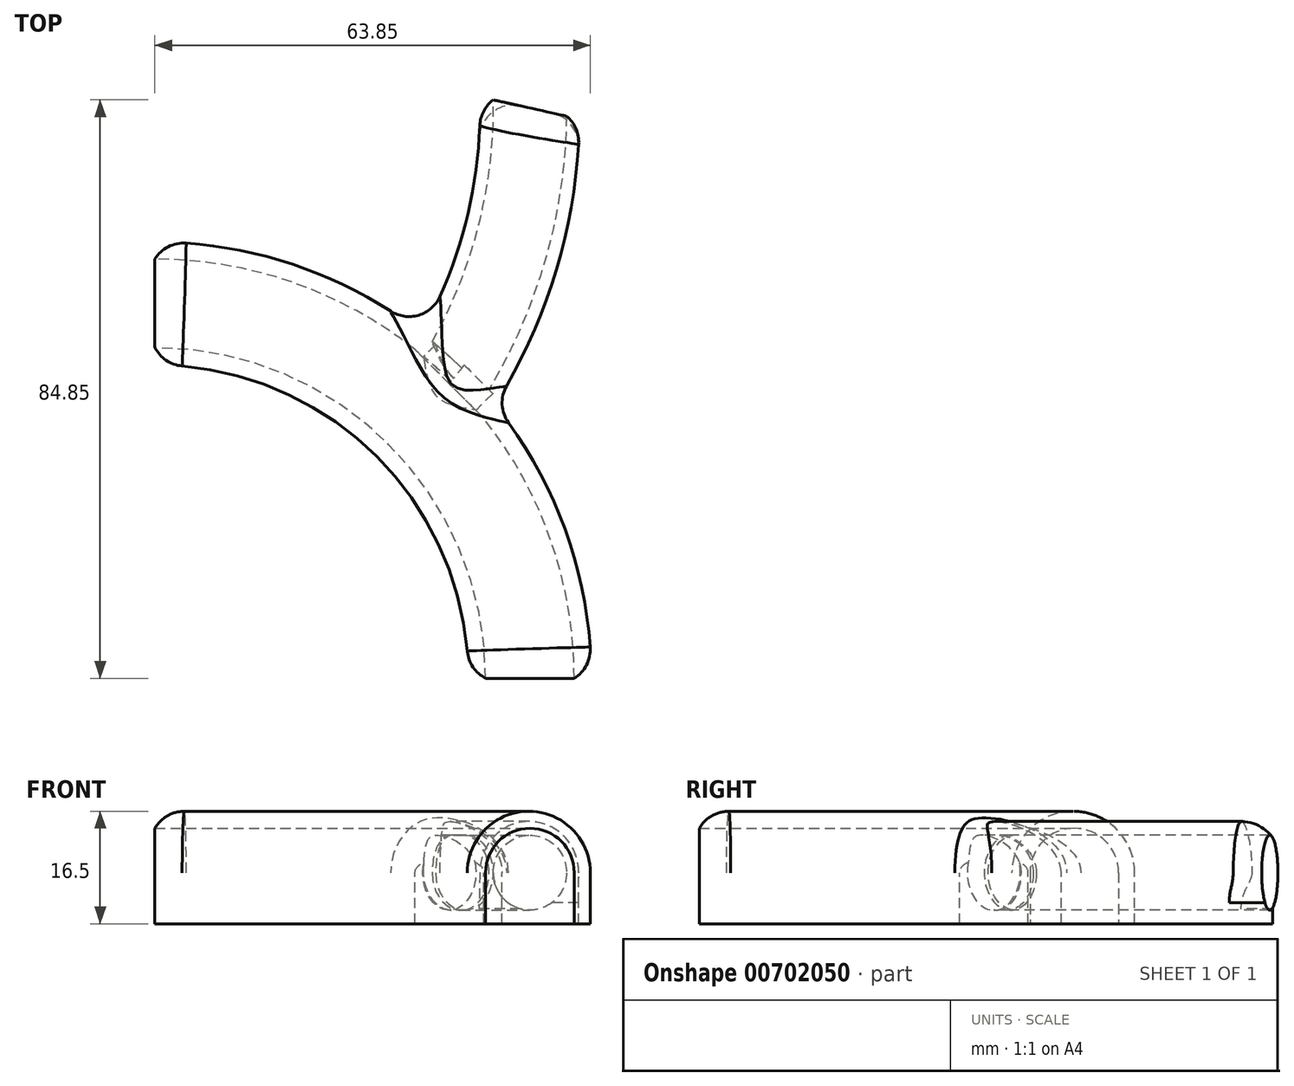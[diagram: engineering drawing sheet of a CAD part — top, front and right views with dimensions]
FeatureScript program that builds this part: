
annotation { "Feature Type Name" : "Feature", "Feature Type Description" : "" }
export const myFeature = defineFeature(function(context is Context, id is Id, definition is map)
    precondition{}
    {
        {
            var Q0;
            Q0=qCreatedBy(makeId("Top.planeOp"),FACE);
            var sketch = newSketch(context, id + "F0", { "sketchPlane" : qUnion([Q0])});
            skArc(sketch, "E0", {"start": v(55, 0) * mm, "mid": v(38.9, 38.9) * mm, "end": v(0, 55) * mm});
            skLineSegment(sketch, "E1", {"start": v(0, 0) * mm, "end": v(43.2, 43.2) * mm, "construction": true});
            skLineSegment(sketch, "E2", {"start": v(55, 0) * mm, "end": v(55, 83.67) * mm, "construction": true});
            skArc(sketch, "E3", {"start": v(43.2, 43.2) * mm, "mid": v(51.99, 62.59) * mm, "end": v(55, 83.67) * mm});
            skSolve(sketch);
        }
        {
            var Q0;
            Q0=qCreatedBy(makeId("Front.planeOp"),FACE);
            var sketch = newSketch(context, id + "F1", { "sketchPlane" : qUnion([Q0])});
            skArc(sketch, "E4", {"start": v(64, 0) * mm, "mid": v(55, 9) * mm, "end": v(46, 0) * mm});
            skLineSegment(sketch, "E5", {"start": v(55, 0) * mm, "end": v(64, 0) * mm, "construction": true});
            skLineSegment(sketch, "E6", {"start": v(55, 0) * mm, "end": v(46, 0) * mm, "construction": true});
            skLineSegment(sketch, "E7", {"start": v(55, 0) * mm, "end": v(55, -9) * mm, "construction": true});
            skLineSegment(sketch, "E8.bottom", {"start": v(46, 0) * mm, "end": v(48.5, 0) * mm});
            skLineSegment(sketch, "E8.left", {"start": v(46, 0) * mm, "end": v(46, -7.5) * mm});
            skArc(sketch, "E9", {"start": v(61.5, 0) * mm, "mid": v(55, 6.5) * mm, "end": v(48.5, 0) * mm});
            skLineSegment(sketch, "E10", {"start": v(55, -7.5) * mm, "end": v(46, -7.5) * mm, "construction": true});
            skLineSegment(sketch, "E11", {"start": v(48.5, 0) * mm, "end": v(48.5, -7.5) * mm});
            skLineSegment(sketch, "E12", {"start": v(48.5, -7.5) * mm, "end": v(46, -7.5) * mm});
            skLineSegment(sketch, "E13.MirrorCS", {"start": v(61.5, 0) * mm, "end": v(61.5, -7.5) * mm});
            skLineSegment(sketch, "E14.MirrorCS", {"start": v(61.5, -7.5) * mm, "end": v(64, -7.5) * mm});
            skLineSegment(sketch, "E15.MirrorCS", {"start": v(64, 0) * mm, "end": v(64, -7.5) * mm});
            skLineSegment(sketch, "E16.trimOffspring", {"start": v(61.5, 0) * mm, "end": v(64, 0) * mm});
            skSolve(sketch);
        }
        {
            var Q0;
            Q0=makeQuery(id+"F1.imprint","IMPRINT",FACE,{"disambiguationData":[TD([[makeQuery(id+"F1.imprint","IMPRINT",EDGE,{"derivedFrom":sQuery(id+"F1.wireOp",EDGE,"E13.MirrorCS")}),1.0]])]});
            var Q1;
            Q1=makeQuery(id+"F1.imprint","IMPRINT",FACE,{"disambiguationData":[TD([[makeQuery(id+"F1.imprint","IMPRINT",EDGE,{"derivedFrom":sQuery(id+"F1.wireOp",EDGE,"E8.bottom")}),-1.0]])]});
            var Q2;
            Q2=makeQuery(id+"F1.imprint","IMPRINT",FACE,{"disambiguationData":[TD([[makeQuery(id+"F1.imprint","IMPRINT",EDGE,{"derivedFrom":sQuery(id+"F1.wireOp",EDGE,"E4")}),1.0]])]});
            var Q3;
            Q3=sQuery(id+"F0.wireOp",EDGE,"E0");
            sweep(context, id + "F2", {"profiles" : qUnion([Q0, Q1, Q2]), "path" : qUnion([Q3])});
        }
        {
            var Q0;
            Q0=sQuery(id+"F0.wireOp",VERTEX,"E1.end");
            var Q1;
            Q1=sQuery(id+"F0.wireOp",EDGE,"E1");
            cPlane(context, id + "F3", {"entities" : qUnion([Q0, Q1]), "cplaneType" : CPlaneType.LINE_POINT, "offset" : 25 * mm, "width" : 150 * mm, "height" : 150 * mm});
        }
        {
            var Q0;
            Q0=qCreatedBy(id+"F3.planeOp",FACE);
            var sketch = newSketch(context, id + "F4", { "sketchPlane" : qUnion([Q0])});
            skArc(sketch, "E17", {"start": v(7.5, 0) * mm, "mid": v(0, 7.5) * mm, "end": v(-7.5, 0) * mm});
            skLineSegment(sketch, "E18", {"start": v(0, 0) * mm, "end": v(7.5, 0) * mm, "construction": true});
            skLineSegment(sketch, "E19", {"start": v(0, 0) * mm, "end": v(-7.5, 0) * mm, "construction": true});
            skLineSegment(sketch, "E20", {"start": v(-7.5, 0) * mm, "end": v(-7.5, -7.5) * mm});
            skLineSegment(sketch, "E21", {"start": v(0, 0) * mm, "end": v(0, -7.5) * mm, "construction": true});
            skLineSegment(sketch, "E22", {"start": v(-7.5, -7.5) * mm, "end": v(0, -7.5) * mm});
            skLineSegment(sketch, "E23.MirrorCS", {"start": v(7.5, -7.5) * mm, "end": v(0, -7.5) * mm});
            skLineSegment(sketch, "E24.MirrorCS", {"start": v(7.5, 0) * mm, "end": v(7.5, -7.5) * mm});
            skCircle(sketch, "E25", {"center": v(0, 0) * mm, "radius": 5.5 * mm});
            skSolve(sketch);
        }
        {
            var Q0;
            Q0=makeQuery(id+"F4.imprint","IMPRINT",FACE,{"disambiguationData":[TD([[makeQuery(id+"F4.imprint","IMPRINT",EDGE,{"derivedFrom":sQuery(id+"F4.wireOp",EDGE,"E17")}),1.0]])]});
            var Q1;
            Q1=sQuery(id+"F4.wireOp",EDGE,"E17");
            var Q2;
            Q2=sQuery(id+"F0.wireOp",EDGE,"E3");
            sweep(context, id + "F5", {"operationType" : NewBodyOperationType.ADD, "profiles" : qUnion([Q0]), "surfaceOperationType" : NewSurfaceOperationType.ADD, "surfaceProfiles" : qUnion([Q1]), "path" : qUnion([Q2])});
        }
        {
            var Q0;
            {var subQ0=sQuery(id+"F4.wireOp",EDGE,"E20");var subQ2=sQuery(id+"F0.wireOp",EDGE,"E0");var subQ3=sQuery(id+"F4.wireOp",EDGE,"E17");var subQ4=sQuery(id+"F4.wireOp",EDGE,"E23.MirrorCS");var subQ5=sQuery(id+"F4.wireOp",EDGE,"E22");var subQ6=sQuery(id+"F4.wireOp",EDGE,"E24.MirrorCS");var subQ7=sQuery(id+"F4.wireOp",EDGE,"E25");Q0=makeQuery(id+"F5.boolean.opBoolean","SPLIT",FACE,{"disambiguationData":[TD([makeQuery(id+"F2.opSweep","SWEPT_FACE",FACE,{"disambiguationData":[OSD([subQ2,sQuery(id+"F1.wireOp",EDGE,"E9")])]})])],"derivedFrom":makeQuery(id+"F5.opSweep","CAP_FACE",FACE,{"disambiguationData":[OSD([sQuery(id+"F0.wireOp",VERTEX,"E3.start"),subQ3,subQ0,subQ5,subQ4,subQ6,subQ7])],"isStart":true})});}
            var sketch = newSketch(context, id + "F6", { "sketchPlane" : qUnion([Q0])});
            skCircle(sketch, "E26", {"center": v(0, 0) * mm, "radius": 5.5 * mm});
            skSolve(sketch);
        }
        {
            var Q0;
            Q0=makeQuery(id+"F5.boolean.opBoolean","INTERSECT",EDGE,{"derivedFrom":[makeQuery(id+"F2.opSweep","SWEPT_FACE",FACE,{"disambiguationData":[OSD([sQuery(id+"F0.wireOp",EDGE,"E0"),sQuery(id+"F1.wireOp",EDGE,"E4")])]}),makeQuery(id+"F5.opSweep","SWEPT_FACE",FACE,{"disambiguationData":[OSD([sQuery(id+"F0.wireOp",EDGE,"E3"),sQuery(id+"F4.wireOp",EDGE,"E17")])]})]});
            var Q1;
            Q1=makeQuery(id+"F2.opSweep","CAP_EDGE",EDGE,{"disambiguationData":[OSD([sQuery(id+"F0.wireOp",VERTEX,"E0.end"),sQuery(id+"F1.wireOp",EDGE,"E4")])],"isStart":false});
            var Q2;
            Q2=makeQuery(id+"F2.opSweep","CAP_EDGE",EDGE,{"disambiguationData":[OSD([sQuery(id+"F0.wireOp",VERTEX,"E0.start"),sQuery(id+"F1.wireOp",EDGE,"E4")])],"isStart":true});
            var Q3;
            Q3=makeQuery(id+"F5.opSweep","CAP_EDGE",EDGE,{"disambiguationData":[OSD([sQuery(id+"F0.wireOp",VERTEX,"E3.end"),sQuery(id+"F4.wireOp",EDGE,"E17")])],"isStart":false});
            fillet(context, id + "F7", {"entities" : qUnion([Q0, Q1, Q2, Q3]), "radius" : 5 * mm, "tangentPropagation" : true, "allowEdgeOverflow" : false});
        }
        {
            var Q0;
            {var subQ0=sQuery(id+"F6.wireOp",EDGE,"E26");Q0=makeQuery(id+"F6.imprint","IMPRINT",FACE,{"disambiguationData":[TD([[makeQuery(id+"F6.imprint","IMPRINT",EDGE,{"disambiguationData":[OD(0.0)],"derivedFrom":subQ0}),1.0]])]});}
            extrude(context, id + "F8", {"entities" : qUnion([Q0]), "operationType" : NewBodyOperationType.REMOVE, "oppositeDirection" : true, "depth" : 7 * mm, "offsetDistance" : 25 * mm, "symmetric" : true});
        }
    });
